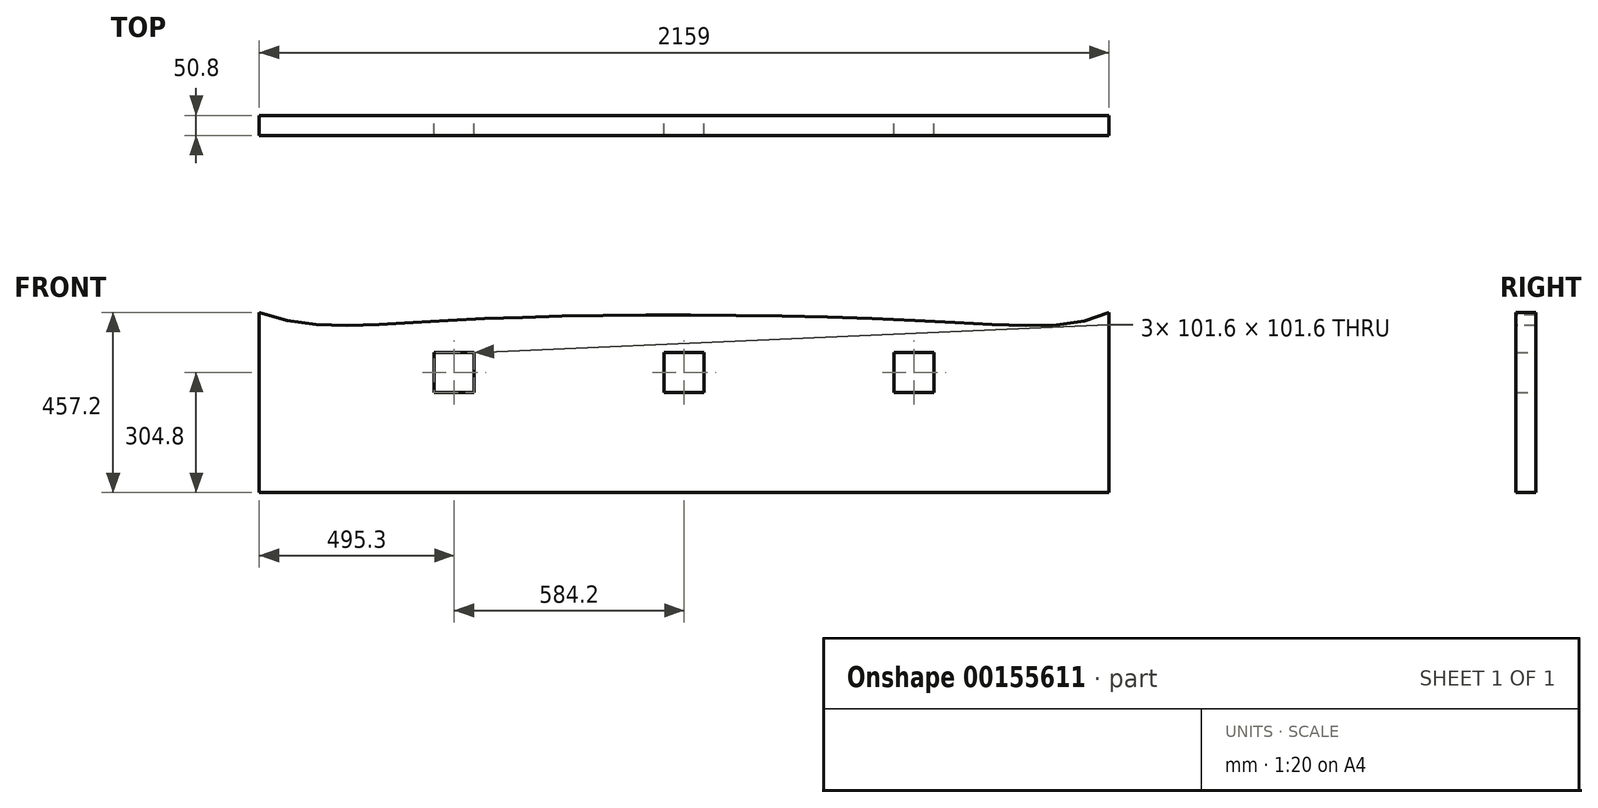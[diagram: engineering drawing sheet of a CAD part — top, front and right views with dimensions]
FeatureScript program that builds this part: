
annotation { "Feature Type Name" : "Feature", "Feature Type Description" : "" }
export const myFeature = defineFeature(function(context is Context, id is Id, definition is map)
    precondition{}
    {
        {
            var Q0;
            Q0=qCreatedBy(makeId("Front.planeOp"),FACE);
            var sketch = newSketch(context, id + "F0", { "sketchPlane" : qUnion([Q0])});
            skLineSegment(sketch, "E0.bottom", {"start": v(-1079.5, 228.6) * mm, "end": v(1079.5, 228.6) * mm});
            skLineSegment(sketch, "E0.top", {"start": v(-1079.5, -228.6) * mm, "end": v(1079.5, -228.6) * mm});
            skLineSegment(sketch, "E0.left", {"start": v(-1079.5, 228.6) * mm, "end": v(-1079.5, -228.6) * mm});
            skLineSegment(sketch, "E0.right", {"start": v(1079.5, 228.6) * mm, "end": v(1079.5, -228.6) * mm});
            skPoint(sketch, "E0.middle", {"position": v(0, 0) * mm});
            skLineSegment(sketch, "E1.bottom", {"start": v(-1079.5, -228.6) * mm, "end": v(-876.3, -228.6) * mm});
            skLineSegment(sketch, "E1.top", {"start": v(-1079.5, -736.6) * mm, "end": v(-876.3, -736.6) * mm});
            skLineSegment(sketch, "E1.left", {"start": v(-1079.5, -228.6) * mm, "end": v(-1079.5, -736.6) * mm});
            skLineSegment(sketch, "E1.right", {"start": v(-876.3, -228.6) * mm, "end": v(-876.3, -736.6) * mm});
            skLineSegment(sketch, "E2.bottom", {"start": v(1079.5, -228.6) * mm, "end": v(876.3, -228.6) * mm});
            skLineSegment(sketch, "E2.top", {"start": v(1079.5, -736.6) * mm, "end": v(876.3, -736.6) * mm});
            skLineSegment(sketch, "E2.left", {"start": v(1079.5, -228.6) * mm, "end": v(1079.5, -736.6) * mm});
            skLineSegment(sketch, "E2.right", {"start": v(876.3, -228.6) * mm, "end": v(876.3, -736.6) * mm});
            skLineSegment(sketch, "E3.bottom", {"start": v(-533.4, 25.4) * mm, "end": v(-635, 25.4) * mm});
            skLineSegment(sketch, "E3.top", {"start": v(-533.4, 127) * mm, "end": v(-635, 127) * mm});
            skLineSegment(sketch, "E3.left", {"start": v(-533.4, 25.4) * mm, "end": v(-533.4, 127) * mm});
            skLineSegment(sketch, "E3.right", {"start": v(-635, 25.4) * mm, "end": v(-635, 127) * mm});
            skPoint(sketch, "E3.middle", {"position": v(-584.2, 76.2) * mm});
            skLineSegment(sketch, "E4.bottom", {"start": v(-50.8, 127) * mm, "end": v(50.8, 127) * mm});
            skLineSegment(sketch, "E4.top", {"start": v(-50.8, 25.4) * mm, "end": v(50.8, 25.4) * mm});
            skLineSegment(sketch, "E4.left", {"start": v(-50.8, 127) * mm, "end": v(-50.8, 25.4) * mm});
            skLineSegment(sketch, "E4.right", {"start": v(50.8, 127) * mm, "end": v(50.8, 25.4) * mm});
            skPoint(sketch, "E4.middle", {"position": v(0, 76.2) * mm});
            skLineSegment(sketch, "E5.bottom", {"start": v(635, 127) * mm, "end": v(533.4, 127) * mm});
            skLineSegment(sketch, "E5.top", {"start": v(635, 25.4) * mm, "end": v(533.4, 25.4) * mm});
            skLineSegment(sketch, "E5.left", {"start": v(635, 127) * mm, "end": v(635, 25.4) * mm});
            skLineSegment(sketch, "E5.right", {"start": v(533.4, 127) * mm, "end": v(533.4, 25.4) * mm});
            skPoint(sketch, "E5.middle", {"position": v(584.2, 76.2) * mm});
            skLineSegment(sketch, "E6.bottom", {"start": v(-1003.3, -381) * mm, "end": v(-952.5, -381) * mm});
            skLineSegment(sketch, "E6.top", {"start": v(-1003.3, -533.4) * mm, "end": v(-952.5, -533.4) * mm});
            skLineSegment(sketch, "E6.left", {"start": v(-1003.3, -381) * mm, "end": v(-1003.3, -533.4) * mm});
            skLineSegment(sketch, "E6.right", {"start": v(-952.5, -381) * mm, "end": v(-952.5, -533.4) * mm});
            skPoint(sketch, "E6.middle", {"position": v(-977.9, -457.2) * mm});
            skLineSegment(sketch, "E7.bottom", {"start": v(952.5, -381) * mm, "end": v(1003.3, -381) * mm});
            skLineSegment(sketch, "E7.top", {"start": v(952.5, -533.4) * mm, "end": v(1003.3, -533.4) * mm});
            skLineSegment(sketch, "E7.left", {"start": v(952.5, -381) * mm, "end": v(952.5, -533.4) * mm});
            skLineSegment(sketch, "E7.right", {"start": v(1003.3, -381) * mm, "end": v(1003.3, -533.4) * mm});
            skPoint(sketch, "E7.middle", {"position": v(977.9, -457.2) * mm});
            skFitSpline(sketch, "E8", {"points": [v(-1079.5, 228.6) * mm, v(-698.5, 203.2) * mm, v(-88.9, 222.25) * mm, v(698.5, 203.2) * mm, v(1079.5, 228.6) * mm], "startDerivative": vector(1569.68, -624.79) * mm, "endDerivative": vector(1366.3, 636.56) * mm});
            skSolve(sketch);
        }
        {
            var Q0;
            Q0=makeQuery(id+"F0.imprint","IMPRINT",FACE,{"disambiguationData":[TD([[makeQuery(id+"F0.imprint","IMPRINT",EDGE,{"derivedFrom":sQuery(id+"F0.wireOp",EDGE,"E1.bottom")}),-1.0]])]});
            var Q1;
            Q1=makeQuery(id+"F0.imprint","IMPRINT",FACE,{"disambiguationData":[TD([[makeQuery(id+"F0.imprint","IMPRINT",EDGE,{"derivedFrom":sQuery(id+"F0.wireOp",EDGE,"E2.bottom")}),1.0]])]});
            var Q2;
            Q2=makeQuery(id+"F0.imprint","IMPRINT",FACE,{"disambiguationData":[TD([[makeQuery(id+"F0.imprint","IMPRINT",EDGE,{"derivedFrom":sQuery(id+"F0.wireOp",EDGE,"E0.top")}),1.0]])]});
            extrude(context, id + "F1", {"entities" : qUnion([Q0, Q1, Q2]), "depth" : 50.8 * mm});
        }
    });
